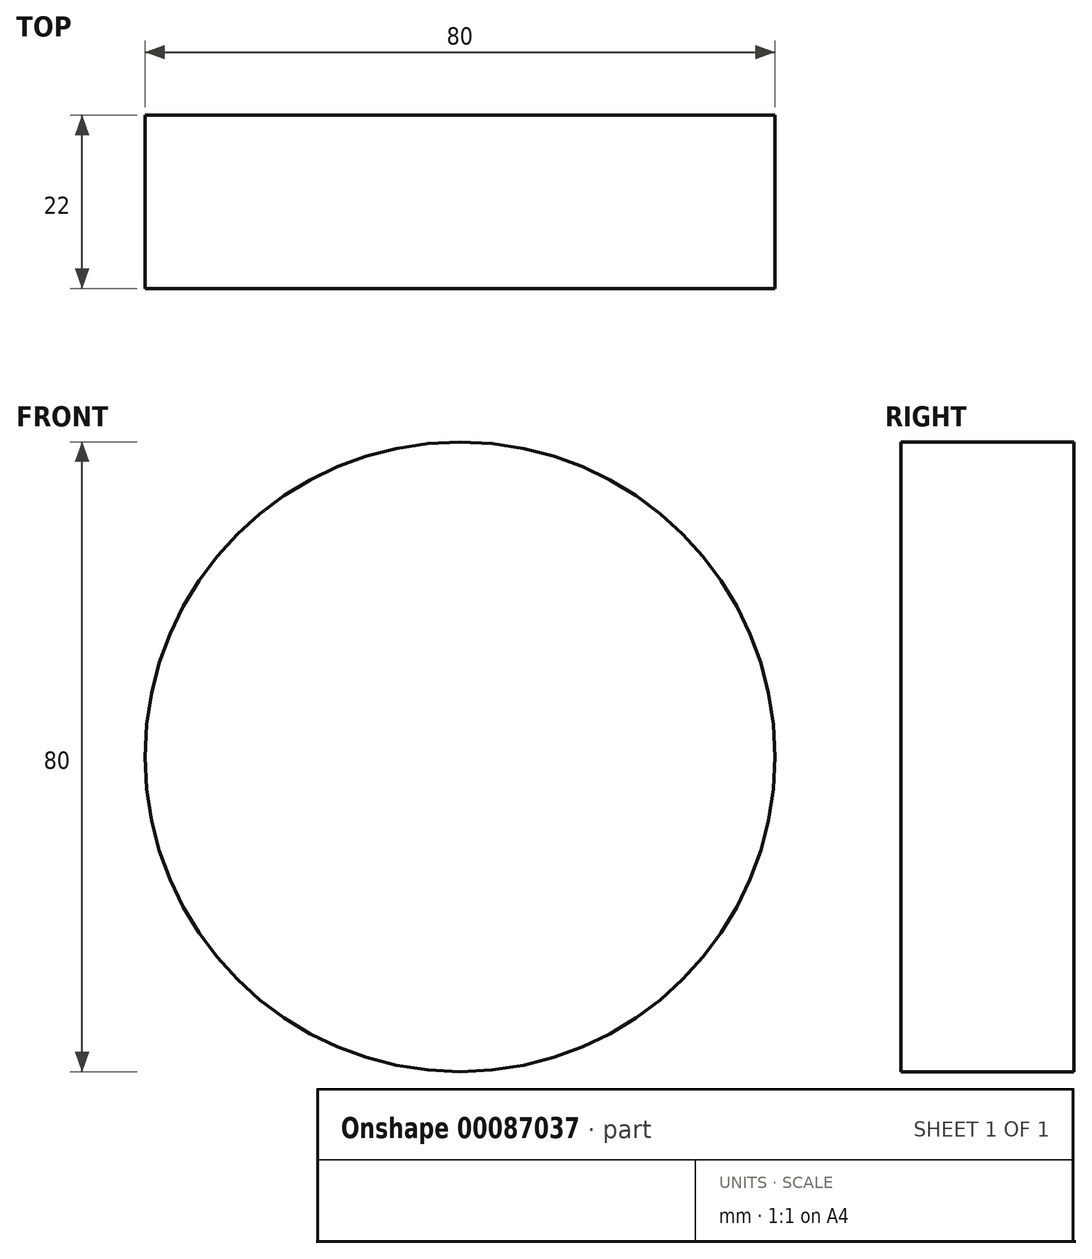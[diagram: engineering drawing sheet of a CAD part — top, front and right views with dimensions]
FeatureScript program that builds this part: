
annotation { "Feature Type Name" : "Feature", "Feature Type Description" : "" }
export const myFeature = defineFeature(function(context is Context, id is Id, definition is map)
    precondition{}
    {
        {
            var Q0;
            Q0=qCreatedBy(makeId("Front.planeOp"),FACE);
            var sketch = newSketch(context, id + "F0", { "sketchPlane" : qUnion([Q0])});
            skCircle(sketch, "E0", {"center": v(0, 0) * mm, "radius": 40 * mm});
            skSolve(sketch);
        }
        {
            var Q0;
            Q0=makeQuery(id+"F0.imprint","IMPRINT",FACE,{"disambiguationData":[TD([[makeQuery(id+"F0.imprint","IMPRINT",EDGE,{"derivedFrom":sQuery(id+"F0.wireOp",EDGE,"E0")}),1.0]])]});
            extrude(context, id + "F1", {"entities" : qUnion([Q0]), "depth" : 22 * mm});
        }
    });
